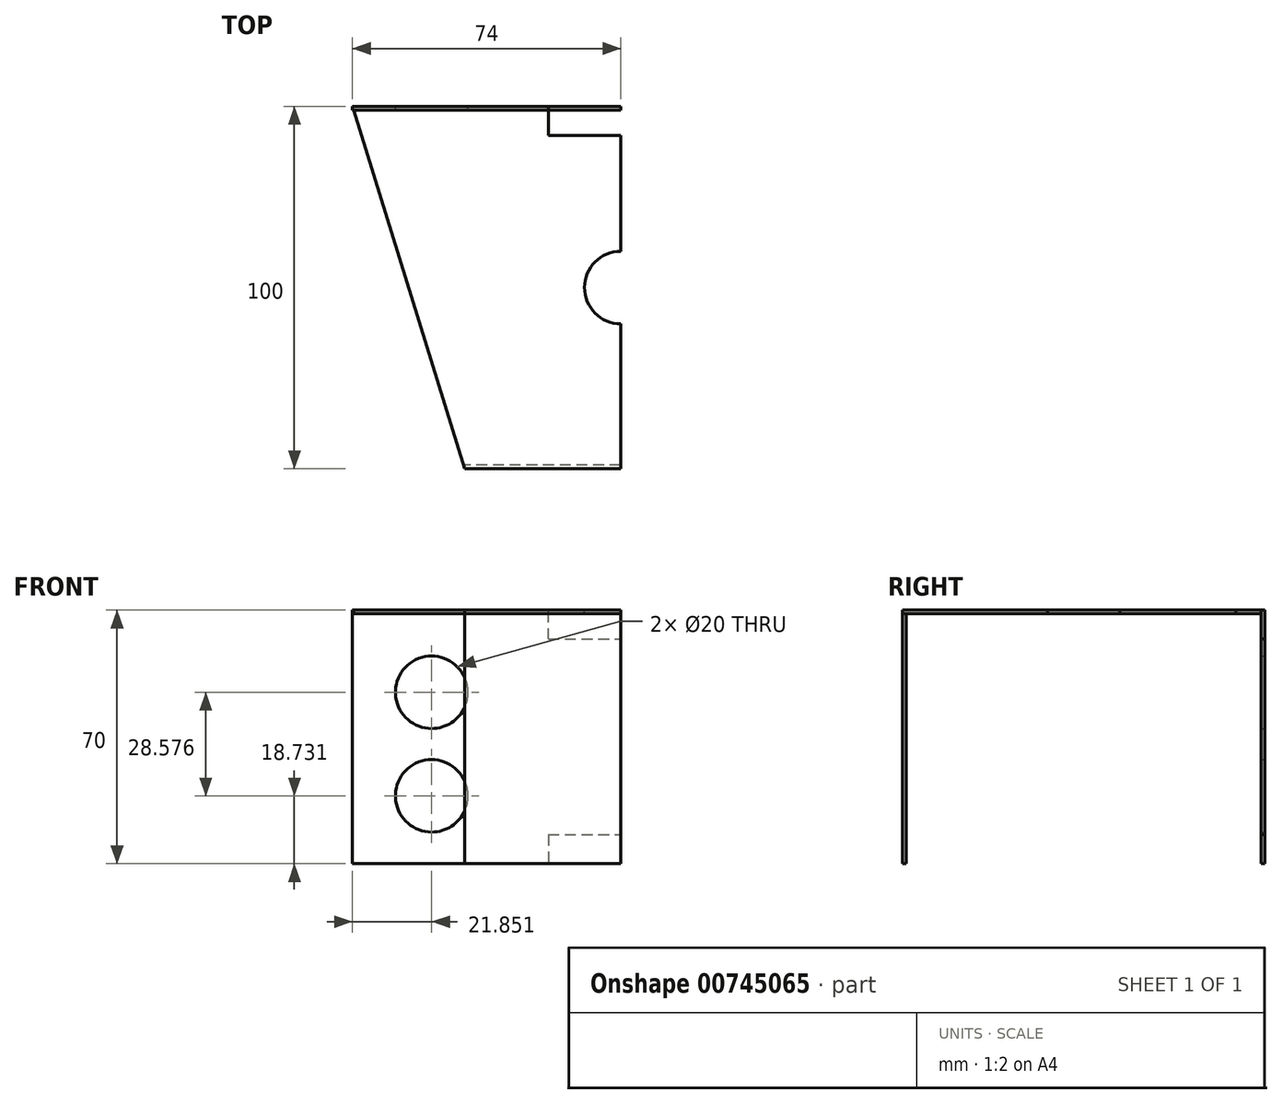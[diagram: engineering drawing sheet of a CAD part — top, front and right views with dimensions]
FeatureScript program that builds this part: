
annotation { "Feature Type Name" : "Feature", "Feature Type Description" : "" }
export const myFeature = defineFeature(function(context is Context, id is Id, definition is map)
    precondition{}
    {
        {
            var Q0;
            Q0=qCreatedBy(makeId("Front.planeOp"),FACE);
            var sketch = newSketch(context, id + "F0", { "sketchPlane" : qUnion([Q0])});
            skLineSegment(sketch, "E0.bottom", {"start": v(17.56, -23.9) * mm, "end": v(37.56, -23.9) * mm});
            skLineSegment(sketch, "E0.top", {"start": v(17.56, 30.1) * mm, "end": v(37.56, 30.1) * mm});
            skLineSegment(sketch, "E0.left", {"start": v(17.56, -23.9) * mm, "end": v(17.56, 30.1) * mm});
            skLineSegment(sketch, "E0.right", {"start": v(37.56, -23.9) * mm, "end": v(37.56, 30.1) * mm});
            skLineSegment(sketch, "E1", {"start": v(17.56, 30.1) * mm, "end": v(17.56, 38.1) * mm});
            skLineSegment(sketch, "E2", {"start": v(17.56, -23.9) * mm, "end": v(17.56, -31.9) * mm});
            skLineSegment(sketch, "E3.bottom", {"start": v(17.56, -31.9) * mm, "end": v(-36.44, -31.9) * mm});
            skLineSegment(sketch, "E3.top", {"start": v(17.56, 38.1) * mm, "end": v(-36.44, 38.1) * mm});
            skLineSegment(sketch, "E3.left", {"start": v(17.56, -31.9) * mm, "end": v(17.56, 38.1) * mm});
            skLineSegment(sketch, "E3.right", {"start": v(-36.44, -31.9) * mm, "end": v(-36.44, 38.1) * mm});
            skLineSegment(sketch, "E4", {"start": v(-14.59, -31.9) * mm, "end": v(-14.59, 38.1) * mm});
            skCircle(sketch, "E5", {"center": v(-14.59, -13.17) * mm, "radius": 10 * mm});
            skCircle(sketch, "E6", {"center": v(-14.59, 15.4) * mm, "radius": 10 * mm});
            skSolve(sketch);
        }
        {
            var Q0;
            Q0 = qSketchRegion(id + "F0", true);
            extrude(context, id + "F1", {"entities" : qUnion([Q0]), "depth" : 1 * mm, "offsetDistance" : 25 * mm});
        }
        {
            var Q0;
            Q0=makeQuery(id+"F1.opExtrude","SWEPT_FACE",FACE,{"disambiguationData":[OSD([sQuery(id+"F0.wireOp",EDGE,"E3.bottom")])]});
            var sketch = newSketch(context, id + "F2", { "sketchPlane" : qUnion([Q0])});
            skLineSegment(sketch, "E7", {"start": v(17.56, 0) * mm, "end": v(17.56, 8) * mm});
            skLineSegment(sketch, "E8", {"start": v(17.56, 8) * mm, "end": v(37.56, 8) * mm});
            skLineSegment(sketch, "E9", {"start": v(37.56, 100) * mm, "end": v(-5.44, 100) * mm});
            skLineSegment(sketch, "E10", {"start": v(-36.44, 0) * mm, "end": v(-5.44, 100) * mm});
            skLineSegment(sketch, "E11", {"start": v(37.56, 8) * mm, "end": v(37.56, 40) * mm});
            skArc(sketch, "E12", {"start": v(37.56, 40) * mm, "mid": v(27.56, 50) * mm, "end": v(37.56, 60) * mm});
            skLineSegment(sketch, "E13", {"start": v(37.56, 60) * mm, "end": v(37.56, 100) * mm});
            skSolve(sketch);
        }
        {
            var Q0;
            Q0=makeQuery(id+"F1.opExtrude","SWEPT_FACE",FACE,{"disambiguationData":[OSD([sQuery(id+"F0.wireOp",EDGE,"E3.top")])]});
            var sketch = newSketch(context, id + "F3", { "sketchPlane" : qUnion([Q0])});
            skLineSegment(sketch, "E14.0.0", {"start": v(-5.44, -100) * mm, "end": v(-36.13, -1) * mm});
            skLineSegment(sketch, "E14.0.1", {"start": v(-36.13, -1) * mm, "end": v(17.56, -1) * mm});
            skLineSegment(sketch, "E14.0.2", {"start": v(17.56, -1) * mm, "end": v(17.56, -8) * mm});
            skLineSegment(sketch, "E14.0.3", {"start": v(17.56, -8) * mm, "end": v(37.56, -8) * mm});
            skLineSegment(sketch, "E14.0.4", {"start": v(37.56, -8) * mm, "end": v(37.56, -40) * mm});
            skArc(sketch, "E14.0.5", {"start": v(37.56, -40) * mm, "mid": v(27.56, -50) * mm, "end": v(37.56, -60) * mm});
            skLineSegment(sketch, "E14.0.6", {"start": v(37.56, -60) * mm, "end": v(37.56, -100) * mm});
            skLineSegment(sketch, "E14.0.7", {"start": v(37.56, -100) * mm, "end": v(-5.44, -100) * mm});
            skSolve(sketch);
        }
        {
            var Q0;
            Q0 = qSketchRegion(id + "F3", true);
            extrude(context, id + "F4", {"entities" : qUnion([Q0]), "oppositeDirection" : true, "depth" : 1 * mm, "offsetDistance" : 25 * mm});
        }
        {
            var Q0;
            Q0=makeQuery(id+"F4.opExtrude","SWEPT_FACE",FACE,{"disambiguationData":[OSD([sQuery(id+"F3.wireOp",EDGE,"E14.0.7")])]});
            var sketch = newSketch(context, id + "F5", { "sketchPlane" : qUnion([Q0])});
            skLineSegment(sketch, "E15.bottom", {"start": v(-5.44, 37.1) * mm, "end": v(37.54, 37.1) * mm});
            skLineSegment(sketch, "E15.top", {"start": v(-5.44, -31.84) * mm, "end": v(37.54, -31.84) * mm});
            skLineSegment(sketch, "E15.left", {"start": v(-5.44, 37.1) * mm, "end": v(-5.44, -31.84) * mm});
            skLineSegment(sketch, "E15.right", {"start": v(37.54, 37.1) * mm, "end": v(37.54, -31.84) * mm});
            skSolve(sketch);
        }
        {
            var Q0;
            Q0 = qSketchRegion(id + "F5", true);
            extrude(context, id + "F6", {"entities" : qUnion([Q0]), "oppositeDirection" : true, "depth" : 1 * mm, "offsetDistance" : 25 * mm});
        }
    });
